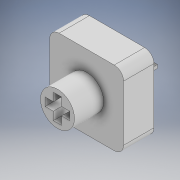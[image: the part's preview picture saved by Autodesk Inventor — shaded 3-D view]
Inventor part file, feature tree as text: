
AUTODESK INVENTOR PART (.ipt)
format: ipt  version: 2022 (Build 260153000, 153)  size: 239,616 bytes
history: native  units: in
note: dims shown in document units (in); Inventor stores cm internally (conversion verified against a paired STEP export)
features: sketch x4, extrude x3, plane x1, projected_geometry x1
ambient origin geometry x8: Origin, YZ Plane, XZ Plane, XY Plane, X Axis, Y Axis, Z Axis, Center Point
bodies: Body1 (feature_tree)
feature tree (9):
  sketch  "Sketch1"  dims[d3=0.2205in d4=0.1594in]
  plane  "Work Plane1"
  sketch  "Sketch2"  dims[d5=0.0531in d6=0.1594in]
  extrude  "Extrusion3"  Depth=0.1594in
  extrude  "Extrusion4"  Depth=0.1594in
  extrude  "Extrusion5"  Depth=0.5016in
  projected_geometry  "Projected Loop1"
  sketch  "Sketch3"  dims[d7=0.0531in d10=0.5016in]
  sketch  "Sketch4"  dims[d12=0.1969in d13=0.0in d14=0.2205in d15=0.1594in d16=0.0531in d17=0.1594in d18=0.0531in d19=0.189in d20=0.0in d21=0.0354in d22=0.0in]
